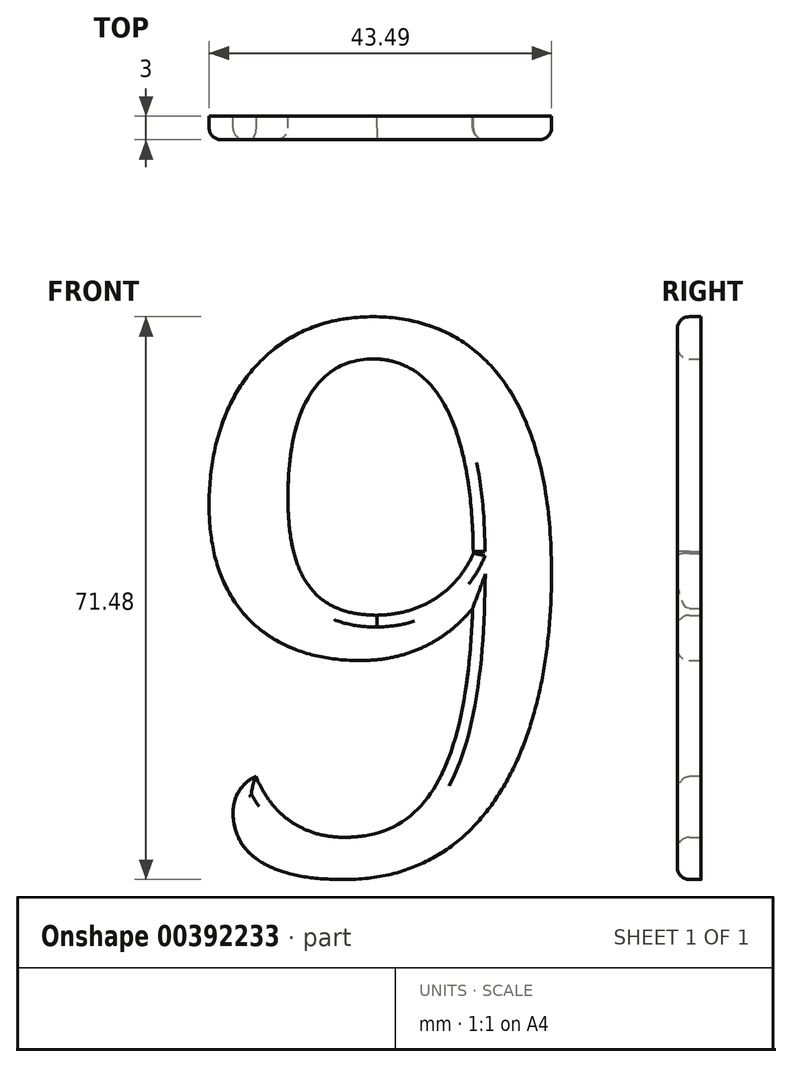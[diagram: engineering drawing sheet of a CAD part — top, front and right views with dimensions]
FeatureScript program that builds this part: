
annotation { "Feature Type Name" : "Feature", "Feature Type Description" : "" }
export const myFeature = defineFeature(function(context is Context, id is Id, definition is map)
    precondition{}
    {
        {
            var Q0;
            Q0=qCreatedBy(makeId("Front.planeOp"),FACE);
            var sketch = newSketch(context, id + "F0", { "sketchPlane" : qUnion([Q0])});
            skText(sketch, "E0", { "text": "9", "fontName": "NotoSerif-Regular.ttf"});
            const initialGuessF0  = {"E0": [0, 0, 1, 0, 0.07]};
            skSetInitialGuess(sketch, initialGuessF0);
            skSolve(sketch);
        }
        {
            var Q0;
            Q0 = qSketchRegion(id + "F0", true);
            extrude(context, id + "F1", {"entities" : qUnion([Q0]), "depth" : 3 * mm});
        }
        {
            var Q0;
            Q0=makeQuery(id+"F1.opExtrude","CAP_FACE",FACE,{"disambiguationData":[OSD([sQuery(id+"F0.wireOp",EDGE,"E0.sketch_text.stroke-0"),sQuery(id+"F0.wireOp",EDGE,"E0.sketch_text.stroke-1"),sQuery(id+"F0.wireOp",EDGE,"E0.sketch_text.stroke-2"),sQuery(id+"F0.wireOp",EDGE,"E0.sketch_text.stroke-3"),sQuery(id+"F0.wireOp",EDGE,"E0.sketch_text.stroke-4"),sQuery(id+"F0.wireOp",EDGE,"E0.sketch_text.stroke-5"),sQuery(id+"F0.wireOp",EDGE,"E0.sketch_text.stroke-6"),sQuery(id+"F0.wireOp",EDGE,"E0.sketch_text.stroke-7"),sQuery(id+"F0.wireOp",EDGE,"E0.sketch_text.stroke-8"),sQuery(id+"F0.wireOp",EDGE,"E0.sketch_text.stroke-9"),sQuery(id+"F0.wireOp",EDGE,"E0.sketch_text.stroke-10"),sQuery(id+"F0.wireOp",EDGE,"E0.sketch_text.stroke-11"),sQuery(id+"F0.wireOp",EDGE,"E0.sketch_text.stroke-12"),sQuery(id+"F0.wireOp",EDGE,"E0.sketch_text.stroke-13"),sQuery(id+"F0.wireOp",EDGE,"E0.sketch_text.stroke-14"),sQuery(id+"F0.wireOp",EDGE,"E0.sketch_text.stroke-15"),sQuery(id+"F0.wireOp",EDGE,"E0.sketch_text.stroke-16"),sQuery(id+"F0.wireOp",EDGE,"E0.sketch_text.stroke-17"),sQuery(id+"F0.wireOp",EDGE,"E0.sketch_text.stroke-18"),sQuery(id+"F0.wireOp",EDGE,"E0.sketch_text.stroke-19"),sQuery(id+"F0.wireOp",EDGE,"E0.sketch_text.stroke-20"),sQuery(id+"F0.wireOp",EDGE,"E0.sketch_text.stroke-21"),sQuery(id+"F0.wireOp",EDGE,"E0.sketch_text.stroke-22"),sQuery(id+"F0.wireOp",EDGE,"E0.sketch_text.stroke-23"),sQuery(id+"F0.wireOp",EDGE,"E0.sketch_text.stroke-24"),sQuery(id+"F0.wireOp",EDGE,"E0.sketch_text.stroke-25"),sQuery(id+"F0.wireOp",EDGE,"E0.sketch_text.stroke-26"),sQuery(id+"F0.wireOp",EDGE,"E0.sketch_text.stroke-27"),sQuery(id+"F0.wireOp",EDGE,"E0.sketch_text.stroke-28"),sQuery(id+"F0.wireOp",EDGE,"E0.sketch_text.stroke-29"),sQuery(id+"F0.wireOp",EDGE,"E0.sketch_text.stroke-30"),sQuery(id+"F0.wireOp",EDGE,"E0.sketch_text.stroke-31"),sQuery(id+"F0.wireOp",EDGE,"E0.sketch_text.stroke-32"),sQuery(id+"F0.wireOp",EDGE,"E0.sketch_text.stroke-33"),sQuery(id+"F0.wireOp",EDGE,"E0.sketch_text.stroke-34"),sQuery(id+"F0.wireOp",EDGE,"E0.sketch_text.stroke-35"),sQuery(id+"F0.wireOp",EDGE,"E0.sketch_text.stroke-36"),sQuery(id+"F0.wireOp",EDGE,"E0.sketch_text.stroke-37"),sQuery(id+"F0.wireOp",EDGE,"E0.sketch_text.stroke-38"),sQuery(id+"F0.wireOp",EDGE,"E0.sketch_text.stroke-39"),sQuery(id+"F0.wireOp",EDGE,"E0.sketch_text.stroke-40"),sQuery(id+"F0.wireOp",EDGE,"E0.sketch_text.stroke-41"),sQuery(id+"F0.wireOp",EDGE,"E0.sketch_text.stroke-42"),sQuery(id+"F0.wireOp",EDGE,"E0.sketch_text.stroke-43"),sQuery(id+"F0.wireOp",EDGE,"E0.sketch_text.stroke-44"),sQuery(id+"F0.wireOp",EDGE,"E0.sketch_text.stroke-45"),sQuery(id+"F0.wireOp",EDGE,"E0.sketch_text.stroke-46"),sQuery(id+"F0.wireOp",EDGE,"E0.sketch_text.stroke-47"),sQuery(id+"F0.wireOp",EDGE,"E0.sketch_text.stroke-48")])],"isStart":false});
            fillet(context, id + "F2", {"entities" : qUnion([Q0]), "radius" : 1.5 * mm, "tangentPropagation" : true, "allowEdgeOverflow" : false});
        }
    });
